# Revit family: 201_ECO1T-_
name_source: partatom
category: Air Terminals
units: mm (PartAtom-declared; Revit-internal decimal feet)

## family parameters
Always vertical = Yes
Cut with Voids When Loaded = No
Part Type = Normal
Room Calculation Point = Yes
Round Connector Dimension = Use Diameter
Shared = No
Work Plane-Based = No

## types (1)
- ECO1T-125
    CAT0 = Yes
    CLBTZ = 0 mm  [stored 0 ft]
    CL_Location_5000 = 5000 mm  [stored 16.4042 ft]
    D = 125 mm
    Description = Room air heating unit. Wall mounting
    H = 158 mm  [stored 0.518373 ft]
    HH = 79 mm  [stored 0.259186 ft]
    H_ARR = 0 mm  [stored 0 ft]
    H__ve = -158 mm  [stored -0.518373 ft]
    LL = 100 mm  [stored 0.328084 ft]
    L_ARR = 400 mm  [stored 1.31234 ft]
    MC_Default_elevation = 0 mm  [stored 0 ft]
    Manufacturer = Climecon
    QmdConnectorList = 201;D
    RX = 41 mm
    URL = www.climecon.fi
    W1 = 24 mm  [stored 0.0787402 ft]
    W_ARR = 400 mm  [stored 1.31234 ft]
    XRefLineVPlnId = 7453
    YRefLineVPlnId = 7456
    magiPartTypeId = 201
    magiProductCode = ECO1T-125
    magiProductFamilyId = ECO1T-*
    magiProductId = ECO1T-125

note: [stored X ft] marks values corroborated as IEEE doubles in the binary element streams (Revit-internal decimal feet)

## geometry (parser evidence)
native form markers: Sweep x2
no freeform markers — native parametric forms only
